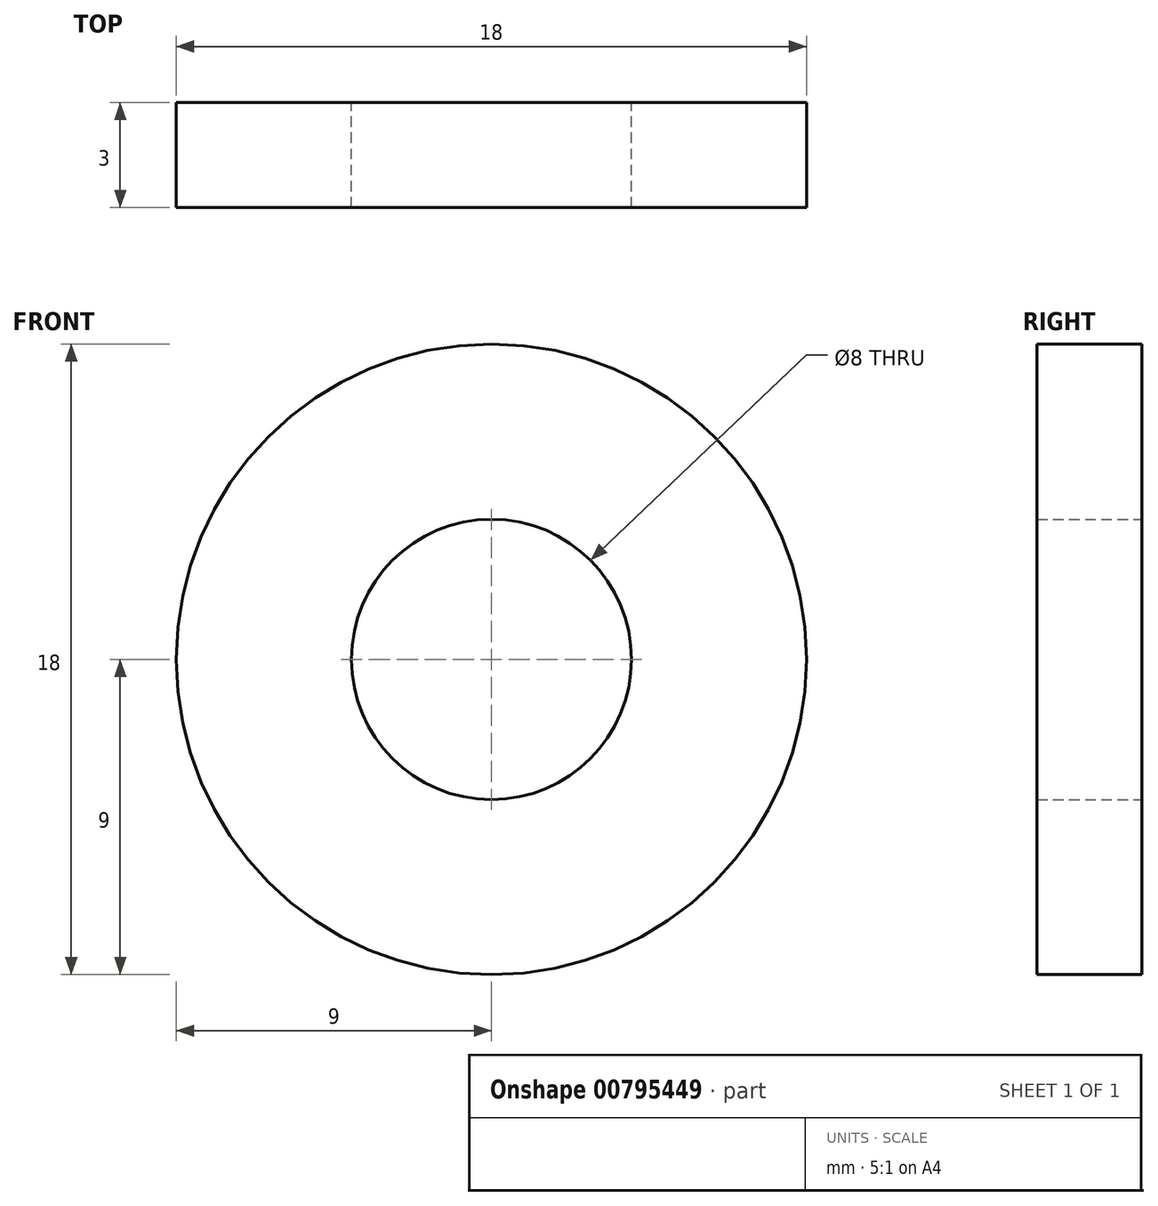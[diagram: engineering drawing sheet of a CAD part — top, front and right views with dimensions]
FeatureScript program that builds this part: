
annotation { "Feature Type Name" : "Feature", "Feature Type Description" : "" }
export const myFeature = defineFeature(function(context is Context, id is Id, definition is map)
    precondition{}
    {
        {
            var Q0;
            Q0=qCreatedBy(makeId("Front.planeOp"),FACE);
            var sketch = newSketch(context, id + "F0", { "sketchPlane" : qUnion([Q0])});
            skCircle(sketch, "E0", {"center": v(0, 0) * mm, "radius": 4 * mm});
            skCircle(sketch, "E1", {"center": v(0, 0) * mm, "radius": 9 * mm});
            skSolve(sketch);
        }
        {
            var Q0;
            Q0=makeQuery(id+"F0.imprint","IMPRINT",FACE,{"disambiguationData":[TD([[makeQuery(id+"F0.imprint","IMPRINT",EDGE,{"derivedFrom":sQuery(id+"F0.wireOp",EDGE,"E0")}),-1.0]])]});
            extrude(context, id + "F1", {"entities" : qUnion([Q0]), "depth" : 3 * mm, "offsetDistance" : 25 * mm});
        }
    });
